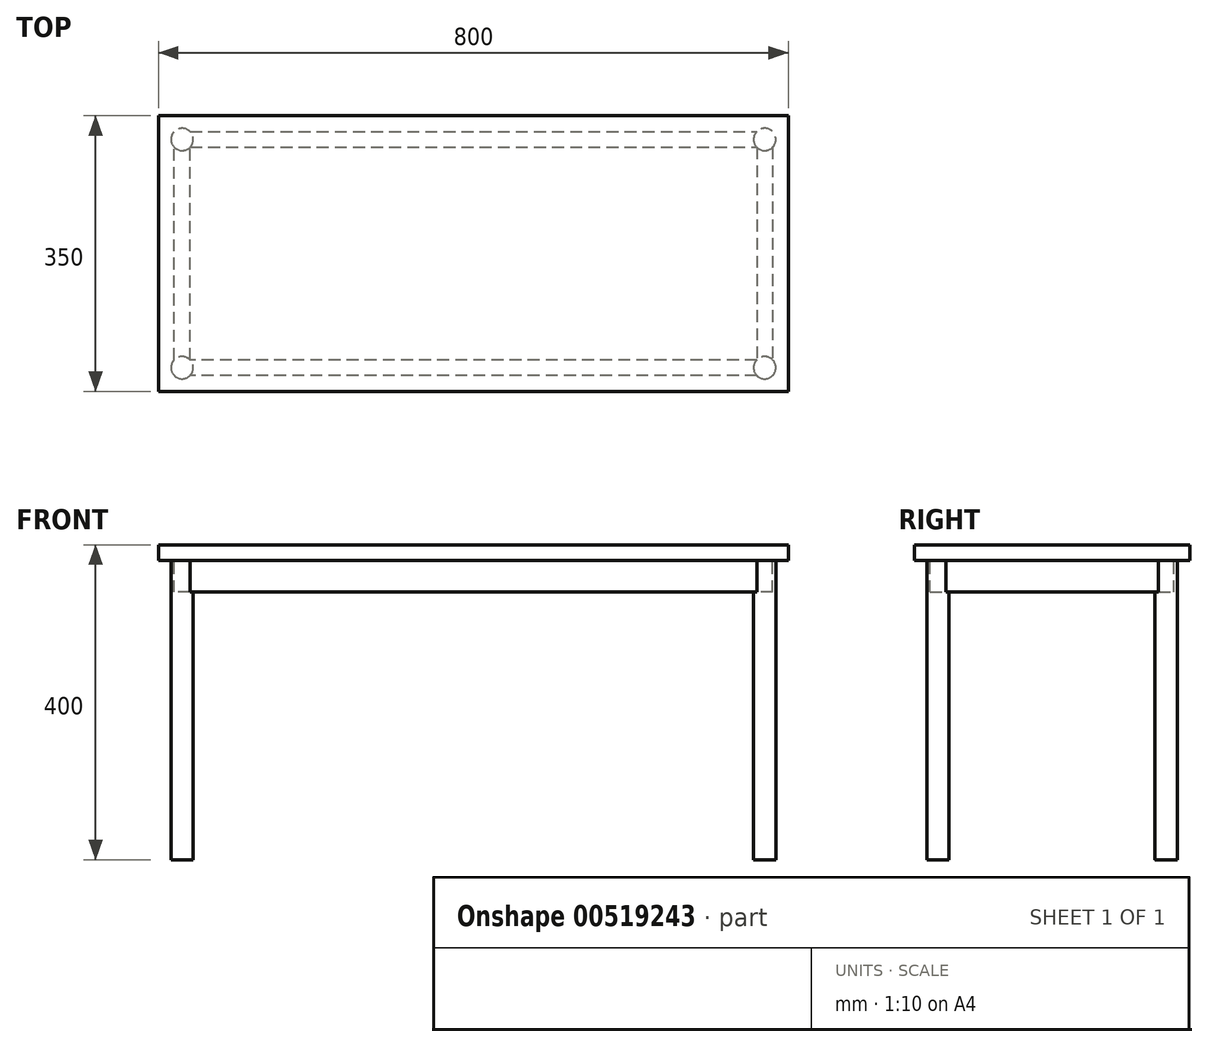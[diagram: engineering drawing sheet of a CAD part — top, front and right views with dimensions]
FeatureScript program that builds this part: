
annotation { "Feature Type Name" : "Feature", "Feature Type Description" : "" }
export const myFeature = defineFeature(function(context is Context, id is Id, definition is map)
    precondition{}
    {
        {
            var Q0;
            Q0=qCreatedBy(makeId("Right.planeOp"),FACE);
            var sketch = newSketch(context, id + "F0", { "sketchPlane" : qUnion([Q0])});
            skLineSegment(sketch, "E0.bottom", {"start": v(0, 0) * mm, "end": v(350, 0) * mm});
            skLineSegment(sketch, "E0.top", {"start": v(0, 20) * mm, "end": v(350, 20) * mm});
            skLineSegment(sketch, "E0.left", {"start": v(0, 0) * mm, "end": v(0, 20) * mm});
            skLineSegment(sketch, "E0.right", {"start": v(350, 0) * mm, "end": v(350, 20) * mm});
            skSolve(sketch);
        }
        {
            var Q0;
            Q0 = qSketchRegion(id + "F0", true);
            extrude(context, id + "F1", {"entities" : qUnion([Q0]), "depth" : 800 * mm, "offsetDistance" : 25 * mm});
        }
        {
            var Q0;
            Q0=makeQuery(id+"F1.opExtrude","SWEPT_FACE",FACE,{"disambiguationData":[OSD([sQuery(id+"F0.wireOp",EDGE,"E0.bottom")])]});
            var sketch = newSketch(context, id + "F2", { "sketchPlane" : qUnion([Q0])});
            skLineSegment(sketch, "E1.0", {"start": v(20, -20) * mm, "end": v(20, -330) * mm});
            skLineSegment(sketch, "E1.1", {"start": v(780, -20) * mm, "end": v(20, -20) * mm});
            skLineSegment(sketch, "E1.2", {"start": v(780, -330) * mm, "end": v(780, -20) * mm});
            skLineSegment(sketch, "E1.3", {"start": v(20, -330) * mm, "end": v(780, -330) * mm});
            skLineSegment(sketch, "E2.0", {"start": v(40, -40) * mm, "end": v(40, -310) * mm});
            skLineSegment(sketch, "E2.1", {"start": v(760, -40) * mm, "end": v(40, -40) * mm});
            skLineSegment(sketch, "E2.2", {"start": v(760, -310) * mm, "end": v(760, -40) * mm});
            skLineSegment(sketch, "E2.3", {"start": v(40, -310) * mm, "end": v(760, -310) * mm});
            skSolve(sketch);
        }
        {
            var Q0;
            Q0 = qSketchRegion(id + "F2", true);
            extrude(context, id + "F3", {"entities" : qUnion([Q0]), "operationType" : NewBodyOperationType.ADD, "depth" : 40 * mm, "offsetDistance" : 25 * mm});
        }
        {
            var Q0;
            {var subQ1=sQuery(id+"F0.wireOp",EDGE,"E0.left");var subQ3=sQuery(id+"F0.wireOp",EDGE,"E0.bottom");Q0=makeQuery(id+"F3.boolean.opBoolean","SPLIT",FACE,{"disambiguationData":[TD([makeQuery(id+"F1.opExtrude","SWEPT_FACE",FACE,{"disambiguationData":[OSD([subQ1])]})])],"derivedFrom":makeQuery(id+"F1.opExtrude","SWEPT_FACE",FACE,{"disambiguationData":[OSD([subQ3])]})});}
            var sketch = newSketch(context, id + "F4", { "sketchPlane" : qUnion([Q0])});
            skLineSegment(sketch, "E3", {"start": v(20, -20) * mm, "end": v(40, -40) * mm, "construction": true});
            skLineSegment(sketch, "E4", {"start": v(400, -20) * mm, "end": v(400, -330) * mm, "construction": true});
            skLineSegment(sketch, "E5", {"start": v(20, -175) * mm, "end": v(780, -175) * mm, "construction": true});
            skCircle(sketch, "E6", {"center": v(30, -30) * mm, "radius": 14.14 * mm});
            skCircle(sketch, "E7.MirrorC", {"center": v(770, -30) * mm, "radius": 14.14 * mm});
            skCircle(sketch, "E8.MirrorC", {"center": v(30, -320) * mm, "radius": 14.14 * mm});
            skCircle(sketch, "E9.MirrorC", {"center": v(770, -320) * mm, "radius": 14.14 * mm});
            skSolve(sketch);
        }
        {
            var Q0;
            Q0 = qSketchRegion(id + "F4", true);
            extrude(context, id + "F5", {"entities" : qUnion([Q0]), "operationType" : NewBodyOperationType.ADD, "depth" : 380 * mm, "offsetDistance" : 25 * mm});
        }
    });
